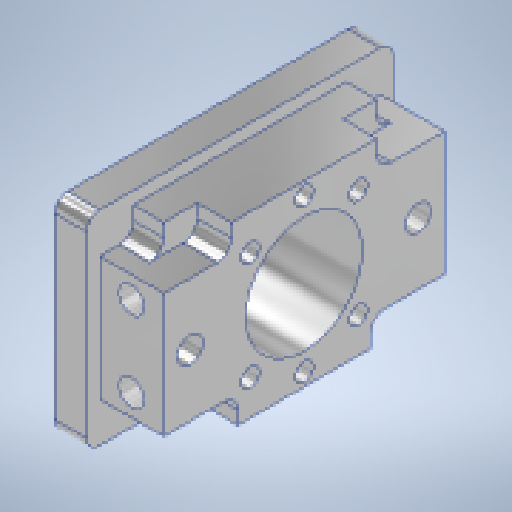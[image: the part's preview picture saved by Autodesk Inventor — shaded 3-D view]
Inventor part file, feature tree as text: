
AUTODESK INVENTOR PART (.ipt)
format: ipt  version: 2025.2 (Build 292293000, 293)  size: 391,168 bytes
history: native  units: mm
features: extrude x6, fillet x2, plane x1, mirror x1
ambient origin geometry x8: Origin, YZ Plane, XZ Plane, XY Plane, X Axis, Y Axis, Z Axis, Center Point
bodies: Solid1 (feature_tree)
feature tree (10):
  extrude  "Extrusion1"  Depth=50.8mm
  extrude  "Extrusion2"  Depth=76.2mm
  plane  "Work Plane1"
  mirror  "Mirror1"
  extrude  "Extrusion4"  Depth=3.175mm
  extrude  "Extrusion5"  Depth=26.5mm
  fillet  "Fillet1"  Radius=10.0mm
  extrude  "Extrusion3"  Depth=16.0mm TaperAngle=0.0deg
  extrude  "Extrusion6"  Depth=16.0mm
  fillet  "Fillet2"  Radius=50.8mm
